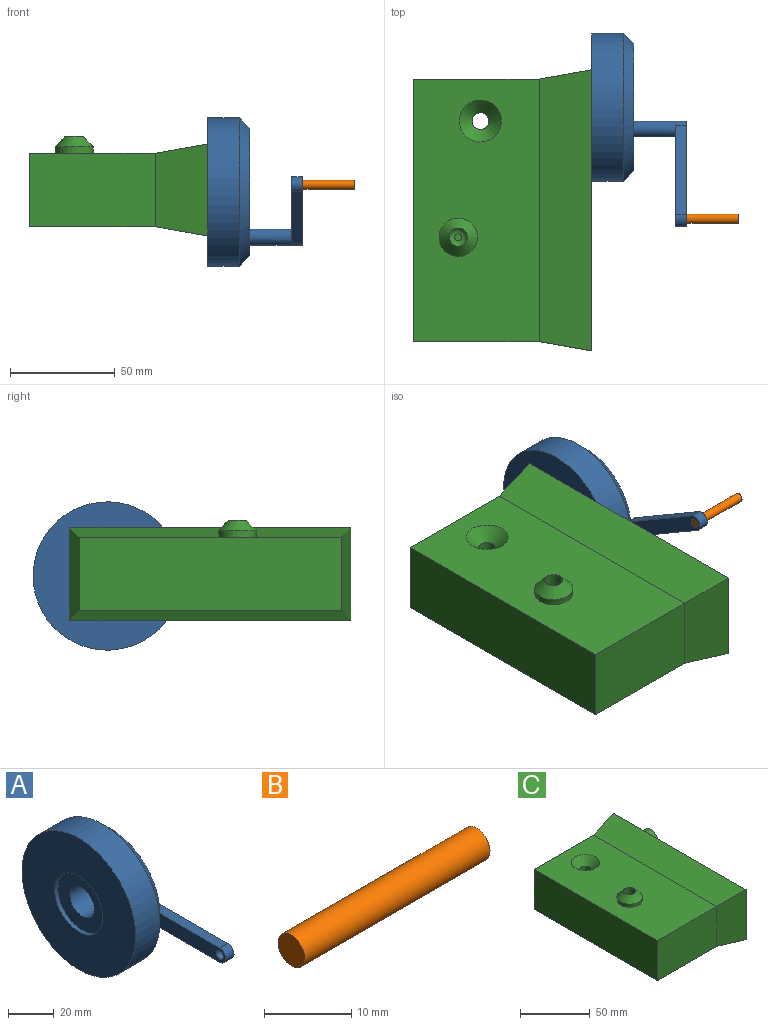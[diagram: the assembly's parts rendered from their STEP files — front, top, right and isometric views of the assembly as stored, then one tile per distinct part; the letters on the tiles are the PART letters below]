
ASSEMBLY  parts=3 mates=2
PART A: 14 faces, bbox 45x86.7x70.6 mm
  f0: cylinder r=3.78mm len=25mm, axis (-1,0,0), area 534.5mm2, adj f3,f7,f9,f10,f12
  f1: cylinder r=7.5mm len=18mm, axis (-1,0,0), area 848.2mm2, adj f3,f6
  f2: cylinder r=35.31mm len=70.63mm, axis (-1,0,0), area 3328.1mm2, adj f4,f13
  f3: plane 60.63x60.63mm, normal (1,0,0), area 2665mm2, adj f0,f1,f13
  f4: plane 70.63x70.63mm, normal (-1,0,0), area 3210.6mm2, adj f2,f5
  f5: cylinder r=15mm len=30mm, axis (-1,0,0), area 188.5mm2, adj f4,f6
  f6: plane 30x30mm, normal (-1,0,0), area 530.1mm2, adj f1,f5
  f7: plane 56.97x7.56mm, normal (1,0,0), area 403.9mm2, adj f0,f8,f9,f10,f11
  f8: cylinder r=3.78mm len=7.56mm, axis (1,0,0), area 59.4mm2, adj f7,f9,f10,f12
  f9: plane 49.41x5mm, normal (0,0,-1), area 247.1mm2, adj f0,f7,f8,f12
  f10: plane 49.41x5mm, normal (0,0,1), area 247.1mm2, adj f0,f7,f8,f12
  f11: cylinder r=2.16mm len=5mm, axis (1,0,0), area 67.9mm2, adj f7,f12
  f12: plane 53.19x7.56mm, normal (-1,0,0), area 359mm2, adj f0,f8,f9,f10,f11
  f13: cone r=30.31mm half-angle=45deg, axis (-1,0,0), area 1457.8mm2, adj f2,f3
PART B: 3 faces, bbox 30x4.3x4.3 mm
  f0: cylinder r=2.16mm len=30mm, axis (-1,0,0), area 407.2mm2, adj f1,f2
  f1: plane 4.32x4.32mm, normal (1,0,0), area 14.7mm2, adj f0
  f2: plane 4.32x4.32mm, normal (-1,0,0), area 14.7mm2, adj f0
PART C: 36 faces, bbox 105x133.8x47.4 mm
  f0: plane 125x35mm, normal (-1,0,0), area 4375mm2, adj f1,f2,f3,f4
  f1: plane 60x35mm, normal (0,-1,0), area 2100mm2, adj f0,f3,f4,f17
  f2: plane 60x35mm, normal (0,1,0), area 2100mm2, adj f0,f3,f4,f15
  f3: plane 125x60mm, normal (0,0,1), area 6932.4mm2, adj f0,f1,f2,f6,f8,f16
  f4: plane 125x60mm, normal (0,0,-1), area 7449.7mm2, adj f0,f1,f2,f5,f14
  f5: cylinder r=4mm len=29mm, axis (0,0,1), area 728.8mm2, adj f4,f6
  f6: cone r=4mm half-angle=45deg, axis (0,0,1), area 373.2mm2, adj f3,f5
  f7: cone r=4.67mm half-angle=3deg, axis (0,0,-1), area 224.3mm2, adj f9,f11
  f8: cone r=8.98mm half-angle=3deg, axis (0,0,1), area 171.4mm2, adj f3,f12
  f9: plane 8.8x8.8mm, normal (0,0,1), area 4.2mm2, adj f7,f12
  f10: plane 3.33x3.33mm, normal (0,0,1), area 8.7mm2, adj f13
  f11: cylinder r=4.67mm len=22mm, axis (0,0,1), area 644.9mm2, adj f7,f13
  f12: cone r=4.4mm half-angle=43.5deg, axis (0,0,-1), area 292.8mm2, adj f8,f9
  f13: torus R=1.67mm, axis (0,0,1), area 105.9mm2, adj f10,f11
  f14: plane 133.82x25mm, normal (-0.17,0,-0.98), area 3285.1mm2, adj f4,f15,f17,f18
  f15: plane 43.82x25mm, normal (-0.17,0.98,0), area 1000.4mm2, adj f2,f14,f16,f18
  f16: plane 133.82x25mm, normal (-0.17,0,0.98), area 3285.1mm2, adj f3,f15,f17,f18
  f17: plane 43.82x25mm, normal (-0.17,-0.98,0), area 1000.4mm2, adj f1,f14,f16,f18
  f18: plane 133.82x43.82mm, normal (1,0,0), area 5686.6mm2, adj f14,f15,f16,f17,f19
  f19: cylinder r=7.5mm len=20mm, axis (-1,0,0), area 942.5mm2, adj f18,f20
  f20: plane 15x15mm, normal (1,0,0), area 176.7mm2, adj f19
  f21: plane 84.52x57.26mm, normal (0,0,-1), area 4258mm2, adj f22,f23,f26,f28,f32,f35
  f22: plane 119x29mm, normal (1,0,0), area 3204.2mm2, adj f21,f23,f24,f35
  f23: plane 57.26x29mm, normal (0,-1,0), area 1660.6mm2, adj f21,f22,f24,f31
  f24: plane 119x57.26mm, normal (0,0,1), area 6660.3mm2, adj f22,f23,f25,f30,f35
  f25: cylinder r=7mm len=24.76mm, axis (0,0,1), area 1088.9mm2, adj f24,f26
  f26: cone r=6.12mm half-angle=45deg, axis (0,0,1), area 343.9mm2, adj f21,f25
  f27: plane 3.33x3.33mm, normal (0,0,-1), area 8.7mm2, adj f29
  f28: cylinder r=7.67mm len=19mm, axis (0,0,1), area 915.1mm2, adj f21,f29
  f29: torus R=1.67mm, axis (0,0,1), area 324.8mm2, adj f27,f28
  f30: plane 126.67x21.74mm, normal (0.17,0,0.98), area 2711.3mm2, adj f24,f31,f33,f34
  f31: plane 36.67x21.74mm, normal (0.17,-0.98,0), area 724.7mm2, adj f23,f30,f32,f34
  f32: plane 126.67x78.41mm, normal (0.17,0,-0.98), area 3438mm2, adj f21,f31,f33,f34,f35
  f33: plane 78.41x36.67mm, normal (0.17,0.98,0), area 1419.4mm2, adj f30,f32,f34,f35
  f34: plane 126.67x36.67mm, normal (-1,0,0), area 4644.3mm2, adj f30,f31,f32,f33
  f35: cylinder r=35mm len=57.26mm, axis (1,0,0), area 1784.6mm2, adj f21,f22,f24,f32,f33
PLACE A rot(axis=(-1,0,0),30.2deg) t=(0,-2.28,24.63)mm
PLACE B rot(axis=(1,0,0),149.8deg) t=(0,-14.97,15.31)mm
PLACE C at identity fixed
MATE fastened A.f8 <-> B.f0  axis (1,0,0) through (65,-8.63,19.97)mm
MATE revolute A.f1 <-> C.f19  axis (-1,0,0) through (45,44.42,16.54)mm
